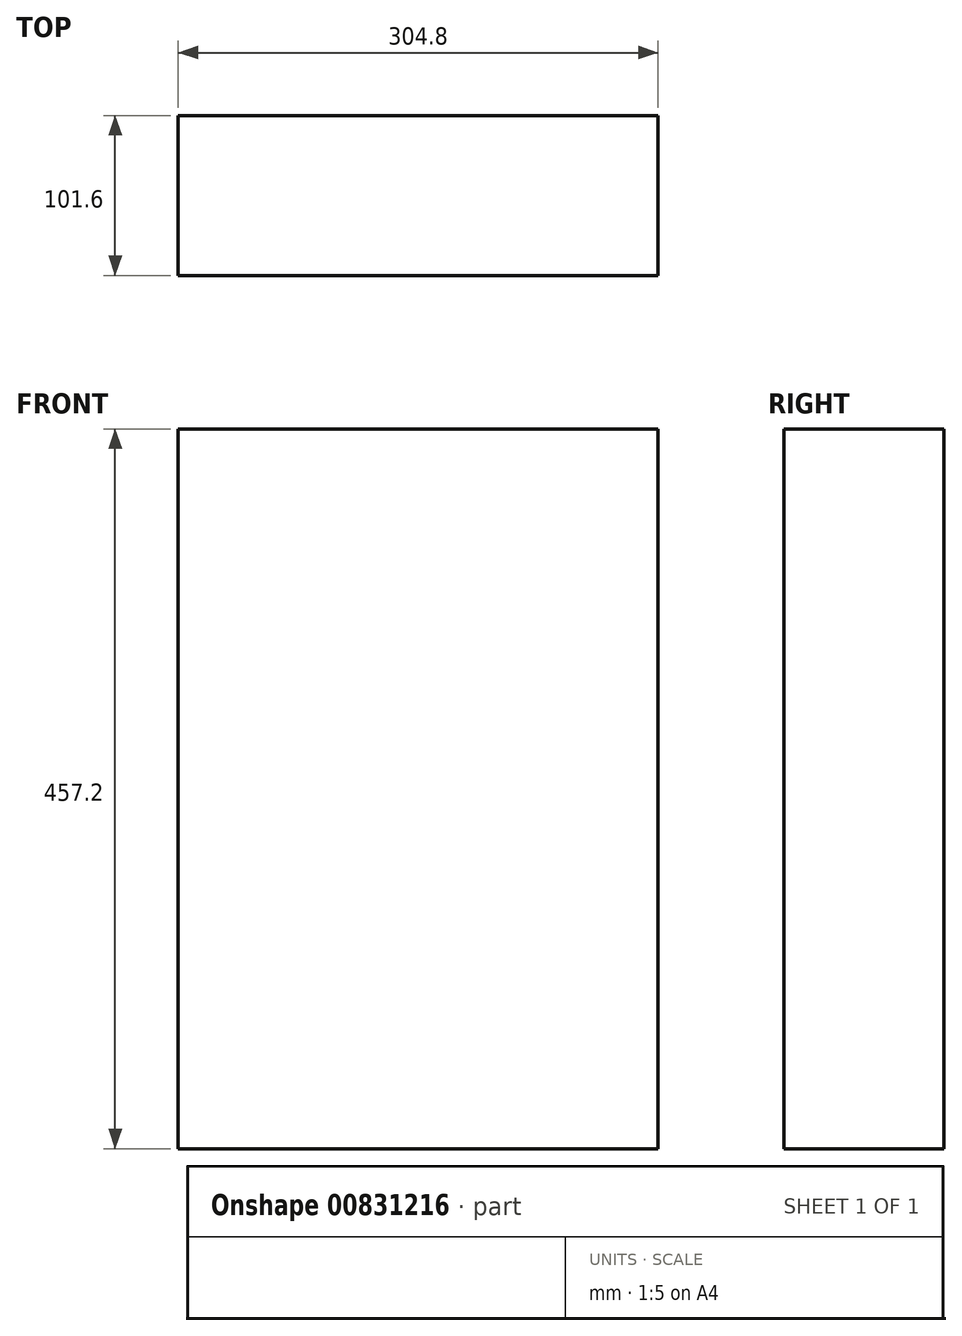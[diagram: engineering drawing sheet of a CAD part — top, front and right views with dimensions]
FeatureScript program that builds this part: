
annotation { "Feature Type Name" : "Feature", "Feature Type Description" : "" }
export const myFeature = defineFeature(function(context is Context, id is Id, definition is map)
    precondition{}
    {
        {
            var Q0;
            Q0=qCreatedBy(makeId("Front.planeOp"),FACE);
            var sketch = newSketch(context, id + "F0", { "sketchPlane" : qUnion([Q0])});
            skLineSegment(sketch, "E0.bottom", {"start": v(152.4, 228.6) * mm, "end": v(-152.4, 228.6) * mm});
            skLineSegment(sketch, "E0.top", {"start": v(152.4, -228.6) * mm, "end": v(-152.4, -228.6) * mm});
            skLineSegment(sketch, "E0.left", {"start": v(152.4, 228.6) * mm, "end": v(152.4, -228.6) * mm});
            skLineSegment(sketch, "E0.right", {"start": v(-152.4, 228.6) * mm, "end": v(-152.4, -228.6) * mm});
            skPoint(sketch, "E0.middle", {"position": v(0, 0) * mm});
            skSolve(sketch);
        }
        {
            var Q0;
            Q0=qSketchRegion(id+"F0",true);
            extrude(context, id + "F1", {"entities" : qUnion([Q0]), "depth" : 101.6 * mm, "offsetDistance" : 25.4 * mm});
        }
    });
